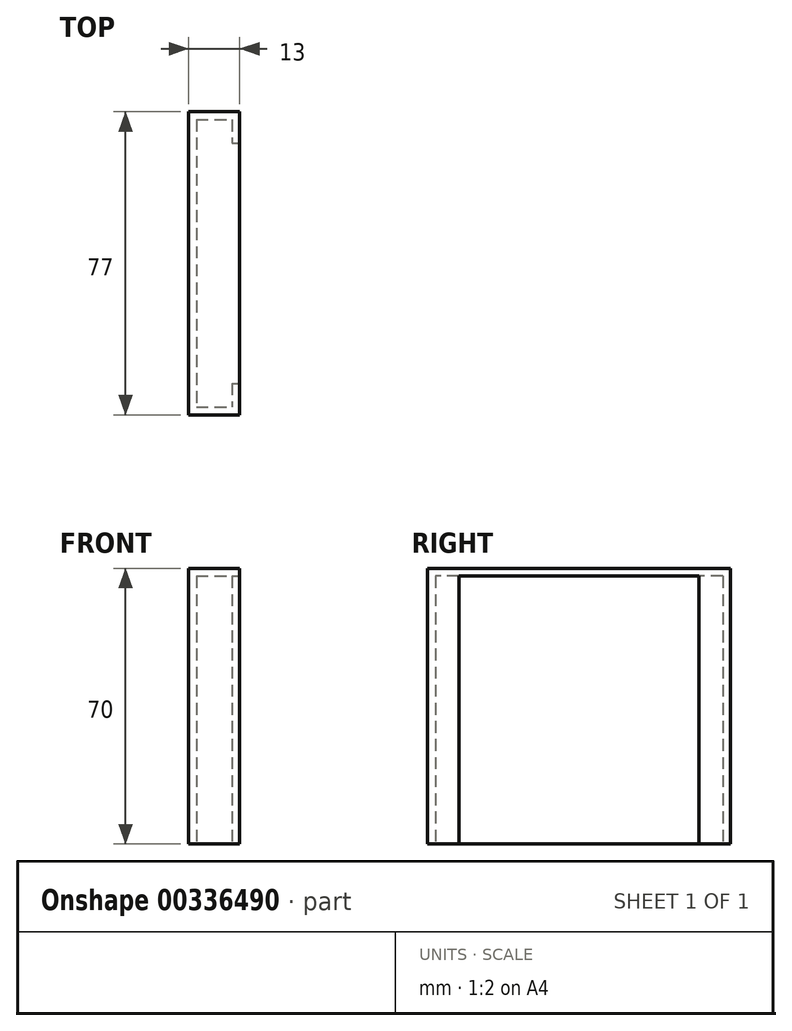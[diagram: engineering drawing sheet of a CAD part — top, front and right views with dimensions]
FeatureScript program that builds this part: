
annotation { "Feature Type Name" : "Feature", "Feature Type Description" : "" }
export const myFeature = defineFeature(function(context is Context, id is Id, definition is map)
    precondition{}
    {
        {
            var Q0;
            Q0=qCreatedBy(makeId("Top.planeOp"),FACE);
            var sketch = newSketch(context, id + "F0", { "sketchPlane" : qUnion([Q0])});
            skLineSegment(sketch, "E0.bottom", {"start": v(-4.5, 36.5) * mm, "end": v(4.5, 36.5) * mm});
            skLineSegment(sketch, "E0.top", {"start": v(-4.5, -36.5) * mm, "end": v(4.5, -36.5) * mm});
            skLineSegment(sketch, "E0.left", {"start": v(-4.5, 36.5) * mm, "end": v(-4.5, -36.5) * mm});
            skLineSegment(sketch, "E0.right", {"start": v(4.5, 36.5) * mm, "end": v(4.5, 30.5) * mm});
            skPoint(sketch, "E0.middle", {"position": v(0, 0) * mm});
            skLineSegment(sketch, "E1.bottom", {"start": v(-6.5, 38.5) * mm, "end": v(6.5, 38.5) * mm});
            skLineSegment(sketch, "E1.top", {"start": v(-6.5, -38.5) * mm, "end": v(6.5, -38.5) * mm});
            skLineSegment(sketch, "E1.left", {"start": v(-6.5, 38.5) * mm, "end": v(-6.5, -38.5) * mm});
            skLineSegment(sketch, "E1.right", {"start": v(6.5, 38.5) * mm, "end": v(6.5, 30.5) * mm});
            skLineSegment(sketch, "E2", {"start": v(4.5, 30.5) * mm, "end": v(6.5, 30.5) * mm});
            skLineSegment(sketch, "E3", {"start": v(4.5, -30.5) * mm, "end": v(6.5, -30.5) * mm});
            skLineSegment(sketch, "E4", {"start": v(6.5, 30.5) * mm, "end": v(6.5, 30.5) * mm});
            skLineSegment(sketch, "E5", {"start": v(4.5, -30.5) * mm, "end": v(4.5, -36.5) * mm});
            skLineSegment(sketch, "E6", {"start": v(6.5, -30.5) * mm, "end": v(6.5, -38.5) * mm});
            skSolve(sketch);
        }
        {
            var Q0;
            Q0=makeQuery(id+"F0.imprint","IMPRINT",FACE,{"disambiguationData":[TD([[makeQuery(id+"F0.imprint","IMPRINT",EDGE,{"derivedFrom":sQuery(id+"F0.wireOp",EDGE,"E0.bottom")}),1.0]])]});
            extrude(context, id + "F1", {"entities" : qUnion([Q0]), "depth" : 70 * mm});
        }
        {
            var Q0;
            Q0=makeQuery(id+"F1.opExtrude","CAP_FACE",FACE,{"disambiguationData":[OSD([sQuery(id+"F0.wireOp",EDGE,"E0.bottom"),sQuery(id+"F0.wireOp",EDGE,"E0.top"),sQuery(id+"F0.wireOp",EDGE,"E0.left"),sQuery(id+"F0.wireOp",EDGE,"E0.right"),sQuery(id+"F0.wireOp",EDGE,"E1.bottom"),sQuery(id+"F0.wireOp",EDGE,"E1.top"),sQuery(id+"F0.wireOp",EDGE,"E1.left"),sQuery(id+"F0.wireOp",EDGE,"E1.right"),sQuery(id+"F0.wireOp",EDGE,"E2"),sQuery(id+"F0.wireOp",EDGE,"E3"),sQuery(id+"F0.wireOp",EDGE,"E5"),sQuery(id+"F0.wireOp",EDGE,"E6"),sQuery(id+"F0.wireOp",EDGE,"rSXkWLr6-CrH9-pdWm-vF5E-HjSM5mUDrRNX.left"),sQuery(id+"F0.wireOp",EDGE,"6l2cuF4d-3lQk-b7m9-tA1l-yx8GFtgZ4TjH.left")])],"isStart":false});
            var sketch = newSketch(context, id + "F2", { "sketchPlane" : qUnion([Q0])});
            skLineSegment(sketch, "E7", {"start": v(6.5, 30.5) * mm, "end": v(6.5, -30.5) * mm});
            skLineSegment(sketch, "E8", {"start": v(6.5, -30.5) * mm, "end": v(4.5, -30.5) * mm});
            skLineSegment(sketch, "E9", {"start": v(4.5, -30.5) * mm, "end": v(4.5, 30.5) * mm});
            skLineSegment(sketch, "E10", {"start": v(4.5, 30.5) * mm, "end": v(-4.5, 30.5) * mm});
            skLineSegment(sketch, "E11", {"start": v(4.5, 17.47) * mm, "end": v(-4.5, 17.47) * mm});
            skLineSegment(sketch, "E12.bottom", {"start": v(108.21, -173.52) * mm, "end": v(82.47, -173.52) * mm});
            skLineSegment(sketch, "E12.top", {"start": v(108.21, -167.52) * mm, "end": v(82.47, -167.52) * mm});
            skLineSegment(sketch, "E12.left", {"start": v(108.21, -173.52) * mm, "end": v(108.21, -167.52) * mm});
            skLineSegment(sketch, "E12.right", {"start": v(82.47, -173.52) * mm, "end": v(82.47, -167.52) * mm});
            skSolve(sketch);
        }
        {
            var Q0;
            Q0=makeQuery(id+"F2.imprint","IMPRINT",FACE,{"disambiguationData":[TD([[makeQuery(id+"F2.imprint","IMPRINT",EDGE,{"derivedFrom":sQuery(id+"F2.wireOp",EDGE,"E7")}),-1.0]])]});
            var Q1;
            {var subQ0=sQuery(id+"F2.wireOp",EDGE,"E10");Q1=makeQuery(id+"F2.imprint","IMPRINT",FACE,{"disambiguationData":[TD([[makeQuery(id+"F2.imprint","IMPRINT",EDGE,{"derivedFrom":subQ0}),1.0]])]});}
            var Q2;
            {var subQ0=sQuery(id+"F2.wireOp",EDGE,"E10");Q2=makeQuery(id+"F2.imprint","IMPRINT",FACE,{"disambiguationData":[TD([[makeQuery(id+"F2.imprint","IMPRINT",EDGE,{"derivedFrom":subQ0}),-1.0]])]});}
            var Q3;
            {var subQ2=sQuery(id+"F2.wireOp",EDGE,"E11");Q3=makeQuery(id+"F2.imprint","IMPRINT",FACE,{"disambiguationData":[TD([[makeQuery(id+"F2.imprint","IMPRINT",EDGE,{"derivedFrom":subQ2}),1.0]])]});}
            extrude(context, id + "F3", {"entities" : qUnion([Q0, Q1, Q2, Q3]), "operationType" : NewBodyOperationType.ADD, "oppositeDirection" : true, "depth" : 2 * mm});
        }
    });
